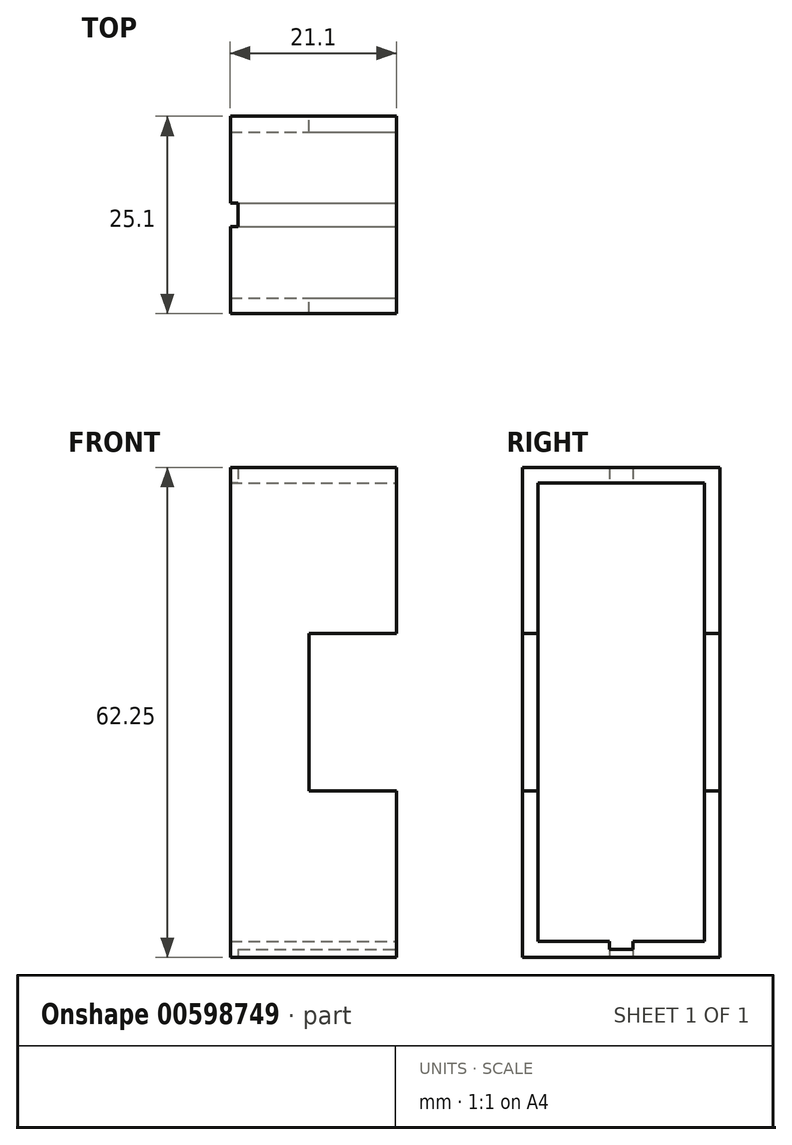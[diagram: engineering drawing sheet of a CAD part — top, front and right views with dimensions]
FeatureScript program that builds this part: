
annotation { "Feature Type Name" : "Feature", "Feature Type Description" : "" }
export const myFeature = defineFeature(function(context is Context, id is Id, definition is map)
    precondition{}
    {
        {
            var Q0;
            Q0=qCreatedBy(makeId("Top.planeOp"),FACE);
            var sketch = newSketch(context, id + "F0", { "sketchPlane" : qUnion([Q0])});
            skLineSegment(sketch, "E0.bottom", {"start": v(11.52, 12.55) * mm, "end": v(-9.58, 12.55) * mm});
            skLineSegment(sketch, "E0.top", {"start": v(11.52, -12.55) * mm, "end": v(-9.58, -12.55) * mm});
            skLineSegment(sketch, "E0.left", {"start": v(11.52, 12.55) * mm, "end": v(11.52, -12.55) * mm});
            skLineSegment(sketch, "E0.right", {"start": v(-9.58, 12.55) * mm, "end": v(-9.58, -12.55) * mm});
            skPoint(sketch, "E0.middle", {"position": v(0.97, 0) * mm});
            skSolve(sketch);
        }
        {
            var Q0;
            Q0=makeQuery(id+"F0.imprint","IMPRINT",FACE,{"disambiguationData":[TD([[makeQuery(id+"F0.imprint","IMPRINT",EDGE,{"derivedFrom":sQuery(id+"F0.wireOp",EDGE,"E0.bottom")}),1.0]])]});
            extrude(context, id + "F1", {"entities" : qUnion([Q0]), "depth" : 62.25 * mm, "offsetDistance" : 25.4 * mm});
        }
        {
            var Q0;
            Q0=makeQuery(id+"F1.opExtrude","SWEPT_FACE",FACE,{"disambiguationData":[OSD([sQuery(id+"F0.wireOp",EDGE,"E0.left")])]});
            var sketch = newSketch(context, id + "F2", { "sketchPlane" : qUnion([Q0])});
            skLineSegment(sketch, "E1.bottom", {"start": v(-10.55, 60.25) * mm, "end": v(10.55, 60.25) * mm});
            skLineSegment(sketch, "E1.top", {"start": v(-10.55, 2) * mm, "end": v(10.55, 2) * mm});
            skLineSegment(sketch, "E1.left", {"start": v(-10.55, 60.25) * mm, "end": v(-10.55, 2) * mm});
            skLineSegment(sketch, "E1.right", {"start": v(10.55, 60.25) * mm, "end": v(10.55, 2) * mm});
            skPoint(sketch, "E1.middle", {"position": v(0, 31.12) * mm});
            skPoint(sketch, "E1.middle.positionSnap0", {"position": v(-12.55, 31.12) * mm});
            skPoint(sketch, "E1.middle.positionSnap1", {"position": v(0, 0) * mm});
            skPoint(sketch, "E1.centerSnap0", {"position": v(-12.55, 31.12) * mm});
            skPoint(sketch, "E1.centerSnap1", {"position": v(0, 0) * mm});
            skSolve(sketch);
        }
        {
            var Q0;
            Q0=makeQuery(id+"F2.imprint","IMPRINT",FACE,{"disambiguationData":[TD([[makeQuery(id+"F2.imprint","IMPRINT",EDGE,{"derivedFrom":sQuery(id+"F2.wireOp",EDGE,"E1.bottom")}),-1.0]])]});
            extrude(context, id + "F3", {"entities" : qUnion([Q0]), "operationType" : NewBodyOperationType.REMOVE, "oppositeDirection" : true, "depth" : 25.4 * mm, "offsetDistance" : 25.4 * mm, "hasSecondDirection" : true, "secondDirectionOppositeDirection" : false, "secondDirectionDepth" : 25.4 * mm});
        }
        {
            var Q0;
            Q0=makeQuery(id+"F1.opExtrude","SWEPT_FACE",FACE,{"disambiguationData":[OSD([sQuery(id+"F0.wireOp",EDGE,"E0.left")])]});
            var sketch = newSketch(context, id + "F4", { "sketchPlane" : qUnion([Q0])});
            skLineSegment(sketch, "E2.bottom", {"start": v(-1.5, 1) * mm, "end": v(1.5, 1) * mm});
            skLineSegment(sketch, "E2.top", {"start": v(-1.5, 3) * mm, "end": v(1.5, 3) * mm});
            skLineSegment(sketch, "E2.left", {"start": v(-1.5, 1) * mm, "end": v(-1.5, 3) * mm});
            skLineSegment(sketch, "E2.right", {"start": v(1.5, 1) * mm, "end": v(1.5, 3) * mm});
            skPoint(sketch, "E2.middle", {"position": v(0, 2) * mm});
            skSolve(sketch);
        }
        {
            var Q0;
            {var subQ0=sQuery(id+"F4.wireOp",EDGE,"E2.bottom");Q0=makeQuery(id+"F4.imprint","IMPRINT",FACE,{"disambiguationData":[TD([[makeQuery(id+"F4.imprint","IMPRINT",EDGE,{"derivedFrom":subQ0}),1.0]])]});}
            extrude(context, id + "F5", {"entities" : qUnion([Q0]), "operationType" : NewBodyOperationType.REMOVE, "oppositeDirection" : true, "depth" : 25.4 * mm, "offsetDistance" : 25.4 * mm, "hasSecondDirection" : true, "secondDirectionOppositeDirection" : false, "secondDirectionDepth" : 25.4 * mm});
        }
        {
            var Q0;
            Q0=makeQuery(id+"F1.opExtrude","SWEPT_FACE",FACE,{"disambiguationData":[OSD([sQuery(id+"F0.wireOp",EDGE,"E0.left")])]});
            var sketch = newSketch(context, id + "F6", { "sketchPlane" : qUnion([Q0])});
            skLineSegment(sketch, "E3.bottom", {"start": v(-12.55, 41.12) * mm, "end": v(12.55, 41.12) * mm});
            skLineSegment(sketch, "E3.top", {"start": v(-12.55, 21.13) * mm, "end": v(12.55, 21.13) * mm});
            skLineSegment(sketch, "E3.left", {"start": v(-12.55, 41.12) * mm, "end": v(-12.55, 21.12) * mm});
            skLineSegment(sketch, "E3.right", {"start": v(12.55, 41.12) * mm, "end": v(12.55, 21.12) * mm});
            skPoint(sketch, "E3.middle", {"position": v(0, 31.13) * mm});
            skPoint(sketch, "E3.middle.positionSnap0", {"position": v(-10.55, 31.13) * mm});
            skPoint(sketch, "E3.centerSnap0", {"position": v(-10.55, 31.13) * mm});
            skSolve(sketch);
        }
        {
            var Q0;
            {var subQ0=sQuery(id+"F6.wireOp",EDGE,"E3.right");Q0=makeQuery(id+"F6.imprint","IMPRINT",FACE,{"disambiguationData":[TD([[makeQuery(id+"F6.imprint","IMPRINT",EDGE,{"derivedFrom":subQ0}),-1.0]])]});}
            var Q1;
            {var subQ0=sQuery(id+"F6.wireOp",EDGE,"E3.left");Q1=makeQuery(id+"F6.imprint","IMPRINT",FACE,{"disambiguationData":[TD([[makeQuery(id+"F6.imprint","IMPRINT",EDGE,{"derivedFrom":subQ0}),1.0]])]});}
            extrude(context, id + "F7", {"entities" : qUnion([Q0, Q1]), "operationType" : NewBodyOperationType.REMOVE, "oppositeDirection" : true, "depth" : 11.1 * mm, "offsetDistance" : 25.4 * mm});
        }
        {
            var Q0;
            Q0=makeQuery(id+"F1.opExtrude","CAP_FACE",FACE,{"disambiguationData":[OSD([sQuery(id+"F0.wireOp",EDGE,"E0.bottom"),sQuery(id+"F0.wireOp",EDGE,"E0.top"),sQuery(id+"F0.wireOp",EDGE,"E0.left"),sQuery(id+"F0.wireOp",EDGE,"E0.right")])],"isStart":true});
            var sketch = newSketch(context, id + "F8", { "sketchPlane" : qUnion([Q0])});
            skLineSegment(sketch, "E4.bottom", {"start": v(-8.58, -1.5) * mm, "end": v(-10.58, -1.5) * mm});
            skLineSegment(sketch, "E4.top", {"start": v(-8.58, 1.5) * mm, "end": v(-10.58, 1.5) * mm});
            skLineSegment(sketch, "E4.left", {"start": v(-8.58, -1.5) * mm, "end": v(-8.58, 1.5) * mm});
            skLineSegment(sketch, "E4.right", {"start": v(-10.58, -1.5) * mm, "end": v(-10.58, 1.5) * mm});
            skPoint(sketch, "E4.middle", {"position": v(-9.58, 0) * mm});
            skSolve(sketch);
        }
        {
            var Q0;
            {var subQ0=sQuery(id+"F8.wireOp",EDGE,"E4.left");Q0=makeQuery(id+"F8.imprint","IMPRINT",FACE,{"disambiguationData":[TD([[makeQuery(id+"F8.imprint","IMPRINT",EDGE,{"derivedFrom":subQ0}),1.0]])]});}
            extrude(context, id + "F9", {"entities" : qUnion([Q0]), "operationType" : NewBodyOperationType.REMOVE, "oppositeDirection" : true, "depth" : 25.4 * mm, "offsetDistance" : 25.4 * mm, "hasSecondDirection" : true, "secondDirectionOppositeDirection" : false, "secondDirectionDepth" : 25.4 * mm});
        }
        {
            var Q0;
            Q0=makeQuery(id+"F3.boolean.opBoolean","COPY",FACE,{"derivedFrom":makeQuery(id+"F3.opExtrude","SWEPT_FACE",FACE,{"disambiguationData":[OSD([sQuery(id+"F2.wireOp",EDGE,"E1.bottom")])]})});
            var sketch = newSketch(context, id + "F10", { "sketchPlane" : qUnion([Q0])});
            skLineSegment(sketch, "E5.bottom", {"start": v(-8.58, 1.5) * mm, "end": v(-10.58, 1.5) * mm});
            skLineSegment(sketch, "E5.top", {"start": v(-8.58, -1.5) * mm, "end": v(-10.58, -1.5) * mm});
            skLineSegment(sketch, "E5.left", {"start": v(-8.58, 1.5) * mm, "end": v(-8.58, -1.5) * mm});
            skLineSegment(sketch, "E5.right", {"start": v(-10.58, 1.5) * mm, "end": v(-10.58, -1.5) * mm});
            skPoint(sketch, "E5.middle", {"position": v(-9.58, 0) * mm});
            skSolve(sketch);
        }
        {
            var Q0;
            {var subQ0=sQuery(id+"F10.wireOp",EDGE,"E5.left");Q0=makeQuery(id+"F10.imprint","IMPRINT",FACE,{"disambiguationData":[TD([[makeQuery(id+"F10.imprint","IMPRINT",EDGE,{"derivedFrom":subQ0}),-1.0]])]});}
            extrude(context, id + "F11", {"entities" : qUnion([Q0]), "operationType" : NewBodyOperationType.REMOVE, "oppositeDirection" : true, "depth" : 25.4 * mm, "offsetDistance" : 25.4 * mm, "hasSecondDirection" : true, "secondDirectionOppositeDirection" : false, "secondDirectionDepth" : 25.4 * mm});
        }
        {
            var Q0;
            Q0=makeQuery(id+"F1.opExtrude","SWEPT_BODY",BODY,{"disambiguationData":[OSD([sQuery(id+"F0.wireOp",EDGE,"E0.bottom"),sQuery(id+"F0.wireOp",EDGE,"E0.top"),sQuery(id+"F0.wireOp",EDGE,"E0.left"),sQuery(id+"F0.wireOp",EDGE,"E0.right")])]});
            transform(context, id + "F12", {"entities" : qUnion([Q0]), "transformType" : TransformType.TRANSLATION_3D, "dx" : 0 * mm, "dy" : 0 * mm, "dz" : 0 * mm, "makeCopy" : true});
        }
        {
            var Q0;
            Q0=makeQuery(id+"F12.opPattern","COPY",BODY,{"derivedFrom":makeQuery(id+"F1.opExtrude","SWEPT_BODY",BODY,{"disambiguationData":[OSD([sQuery(id+"F0.wireOp",EDGE,"E0.bottom"),sQuery(id+"F0.wireOp",EDGE,"E0.top"),sQuery(id+"F0.wireOp",EDGE,"E0.left"),sQuery(id+"F0.wireOp",EDGE,"E0.right")])]}),"instanceName":"1"});
            deleteBodies(context, id + "F13", {"entities" : qUnion([Q0])});
        }
    });
